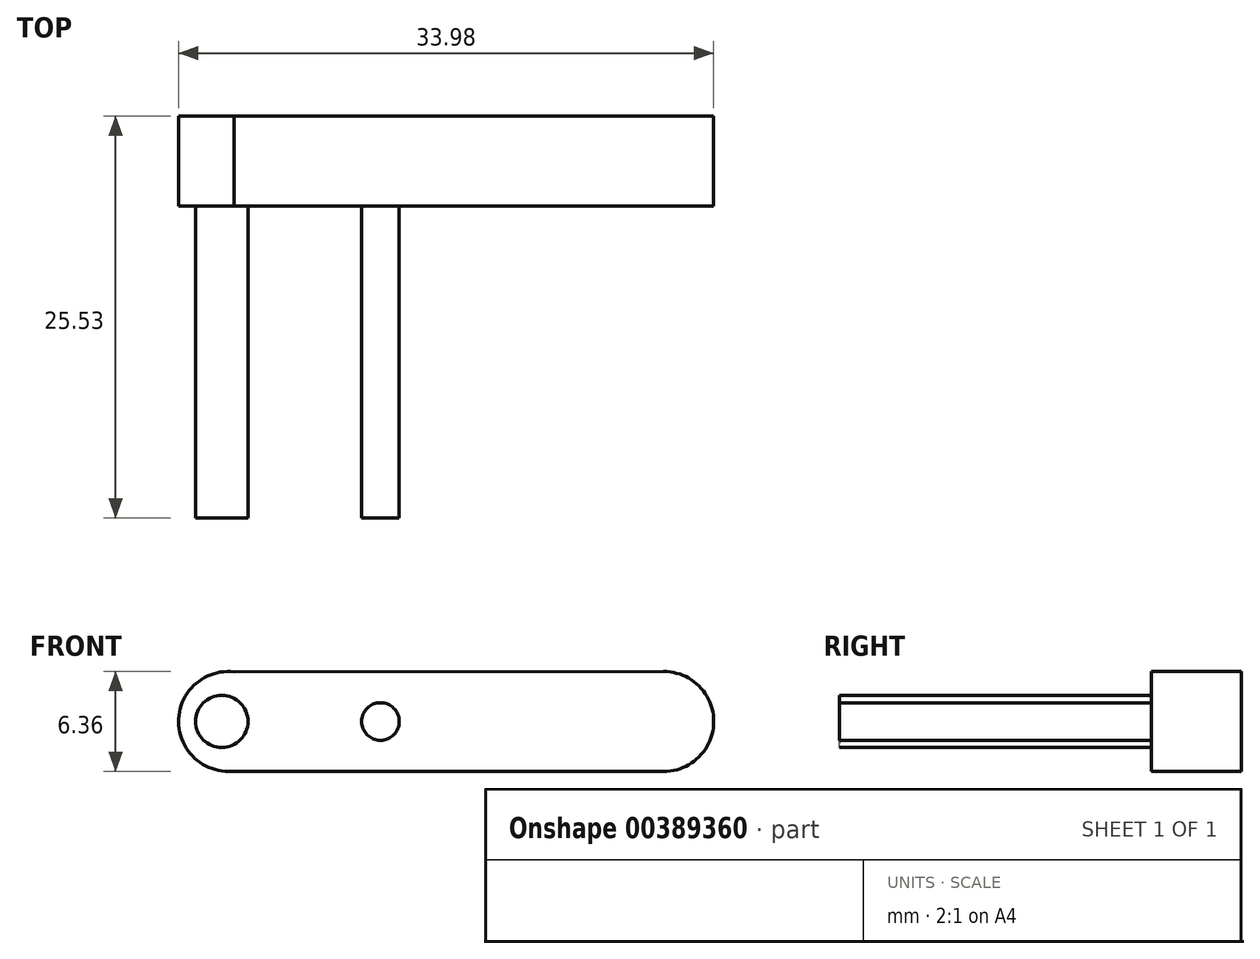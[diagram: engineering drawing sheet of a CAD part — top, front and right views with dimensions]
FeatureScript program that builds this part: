
annotation { "Feature Type Name" : "Feature", "Feature Type Description" : "" }
export const myFeature = defineFeature(function(context is Context, id is Id, definition is map)
    precondition{}
    {
        {
            var Q0;
            Q0=qCreatedBy(makeId("Front.planeOp"),FACE);
            var sketch = newSketch(context, id + "F0", { "sketchPlane" : qUnion([Q0])});
            skArc(sketch, "E0", {"start": v(-52.05, 3.16) * mm, "mid": v(-55.56, 0.17) * mm, "end": v(-52.39, -3.18) * mm});
            skArc(sketch, "E1", {"start": v(-24.75, -3.18) * mm, "mid": v(-21.58, 0) * mm, "end": v(-24.76, 3.17) * mm});
            skLineSegment(sketch, "E2", {"start": v(-52.05, 3.16) * mm, "end": v(-24.75, 3.18) * mm});
            skLineSegment(sketch, "E3", {"start": v(-52.39, -3.18) * mm, "end": v(-24.75, -3.18) * mm});
            skSolve(sketch);
        }
        {
            var Q0;
            {var subQ0=sQuery(id+"F0.wireOp",EDGE,"E0");Q0=makeQuery(id+"F0.imprint","IMPRINT",FACE,{"disambiguationData":[TD([[makeQuery(id+"F0.imprint","IMPRINT",EDGE,{"derivedFrom":subQ0}),1.0]])]});}
            extrude(context, id + "F1", {"entities" : qUnion([Q0]), "depth" : 5.7 * mm});
        }
        {
            var Q0;
            Q0=makeQuery(id+"F1.opExtrude","CAP_FACE",FACE,{"disambiguationData":[OSD([sQuery(id+"F0.wireOp",EDGE,"E0"),sQuery(id+"F0.wireOp",EDGE,"E1"),sQuery(id+"F0.wireOp",EDGE,"E2"),sQuery(id+"F0.wireOp",EDGE,"E3")])],"isStart":false});
            var sketch = newSketch(context, id + "F2", { "sketchPlane" : qUnion([Q0])});
            skCircle(sketch, "E4", {"center": v(-52.82, 0) * mm, "radius": 1.66 * mm});
            skCircle(sketch, "E5", {"center": v(-42.74, 0) * mm, "radius": 1.2 * mm});
            skCircle(sketch, "E6", {"center": v(-27.51, 0) * mm, "radius": 1.2 * mm});
            skSolve(sketch);
        }
        {
            var Q0;
            Q0=makeQuery(id+"F2.imprint","IMPRINT",FACE,{"disambiguationData":[TD([[makeQuery(id+"F2.imprint","IMPRINT",EDGE,{"derivedFrom":sQuery(id+"F2.wireOp",EDGE,"E4")}),1.0]])]});
            var Q1;
            Q1=makeQuery(id+"F2.imprint","IMPRINT",FACE,{"disambiguationData":[TD([[makeQuery(id+"F2.imprint","IMPRINT",EDGE,{"derivedFrom":sQuery(id+"F2.wireOp",EDGE,"E5")}),1.0]])]});
            extrude(context, id + "F3", {"entities" : qUnion([Q0, Q1]), "operationType" : NewBodyOperationType.ADD, "depth" : 19.8 * mm});
        }
    });
